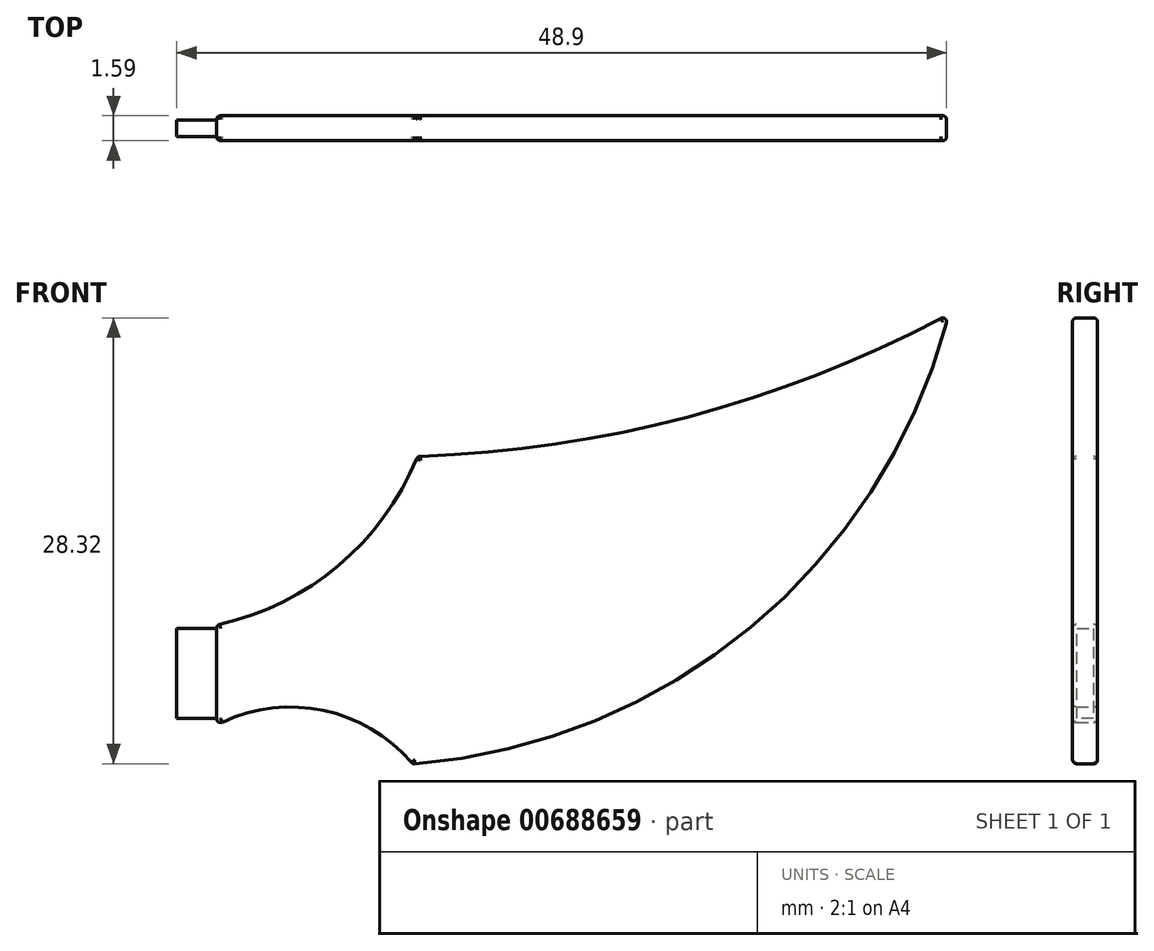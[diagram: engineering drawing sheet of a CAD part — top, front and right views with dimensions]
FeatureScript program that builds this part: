
annotation { "Feature Type Name" : "Feature", "Feature Type Description" : "" }
export const myFeature = defineFeature(function(context is Context, id is Id, definition is map)
    precondition{}
    {
        {
            var Q0;
            Q0=qCreatedBy(makeId("Front.planeOp"),FACE);
            var sketch = newSketch(context, id + "F0", { "sketchPlane" : qUnion([Q0])});
            skLineSegment(sketch, "E0", {"start": v(0, 0) * mm, "end": v(0, 6.35) * mm});
            skLineSegment(sketch, "E1", {"start": v(0, 6.35) * mm, "end": v(12.77, 17.06) * mm, "construction": true});
            skLineSegment(sketch, "E2", {"start": v(12.77, 17.06) * mm, "end": v(46.5, 26.1) * mm, "construction": true});
            skLineSegment(sketch, "E3", {"start": v(12.77, 17.06) * mm, "end": v(12.77, 6.6) * mm, "construction": true});
            skLineSegment(sketch, "E4", {"start": v(46.5, 26.1) * mm, "end": v(12.45, -2.47) * mm, "construction": true});
            skLineSegment(sketch, "E5", {"start": v(46.5, 26.1) * mm, "end": v(46.5, 12.28) * mm, "construction": true});
            skLineSegment(sketch, "E6", {"start": v(0, 0) * mm, "end": v(12.45, -2.47) * mm, "construction": true});
            skArc(sketch, "E7", {"start": v(0, 6.35) * mm, "mid": v(7.72, 10.12) * mm, "end": v(12.77, 17.06) * mm});
            skArc(sketch, "E8", {"start": v(12.77, 17.06) * mm, "mid": v(30.16, 19.63) * mm, "end": v(46.5, 26.1) * mm});
            skArc(sketch, "E9", {"start": v(12.45, -2.47) * mm, "mid": v(34.08, 6.34) * mm, "end": v(46.5, 26.1) * mm});
            skArc(sketch, "E10", {"start": v(12.45, -2.47) * mm, "mid": v(6.66, 0.95) * mm, "end": v(0, 0) * mm});
            skSolve(sketch);
        }
        {
            var Q0;
            Q0=makeQuery(id+"F0.imprint","IMPRINT",FACE,{"disambiguationData":[TD([[makeQuery(id+"F0.imprint","IMPRINT",EDGE,{"derivedFrom":sQuery(id+"F0.wireOp",EDGE,"E0")}),-1.0]])]});
            extrude(context, id + "F1", {"entities" : qUnion([Q0]), "depth" : 1.59 * mm, "offsetDistance" : 25.4 * mm});
        }
        {
            var Q0;
            Q0=makeQuery(id+"F1.opExtrude","CAP_EDGE",EDGE,{"disambiguationData":[OSD([sQuery(id+"F0.wireOp",EDGE,"E7")])],"isStart":true});
            var Q1;
            Q1=makeQuery(id+"F1.opExtrude","CAP_EDGE",EDGE,{"disambiguationData":[OSD([sQuery(id+"F0.wireOp",EDGE,"E7")])],"isStart":false});
            var Q2;
            Q2=makeQuery(id+"F1.opExtrude","CAP_FACE",FACE,{"disambiguationData":[OSD([sQuery(id+"F0.wireOp",EDGE,"E0"),sQuery(id+"F0.wireOp",EDGE,"E7"),sQuery(id+"F0.wireOp",EDGE,"E8"),sQuery(id+"F0.wireOp",EDGE,"E9"),sQuery(id+"F0.wireOp",EDGE,"E10")])],"isStart":true});
            var Q3;
            Q3=makeQuery(id+"F1.opExtrude","CAP_FACE",FACE,{"disambiguationData":[OSD([sQuery(id+"F0.wireOp",EDGE,"E0"),sQuery(id+"F0.wireOp",EDGE,"E7"),sQuery(id+"F0.wireOp",EDGE,"E8"),sQuery(id+"F0.wireOp",EDGE,"E9"),sQuery(id+"F0.wireOp",EDGE,"E10")])],"isStart":false});
            fillet(context, id + "F2", {"entities" : qUnion([Q0, Q1, Q2, Q3]), "radius" : 0.25 * mm, "tangentPropagation" : true, "allowEdgeOverflow" : false});
        }
        {
            var Q0;
            Q0=makeQuery(id+"F1.opExtrude","SWEPT_EDGE",EDGE,{"disambiguationData":[OSD([sQuery(id+"F0.wireOp",EDGE,"E0"),sQuery(id+"F0.wireOp",EDGE,"E7")])]});
            var Q1;
            Q1=makeQuery(id+"F1.opExtrude","SWEPT_EDGE",EDGE,{"disambiguationData":[OSD([sQuery(id+"F0.wireOp",EDGE,"E0"),sQuery(id+"F0.wireOp",EDGE,"E10")])]});
            var Q2;
            Q2=makeQuery(id+"F1.opExtrude","SWEPT_EDGE",EDGE,{"disambiguationData":[OSD([sQuery(id+"F0.wireOp",EDGE,"E9"),sQuery(id+"F0.wireOp",EDGE,"E10")])]});
            var Q3;
            Q3=makeQuery(id+"F1.opExtrude","SWEPT_EDGE",EDGE,{"disambiguationData":[OSD([sQuery(id+"F0.wireOp",EDGE,"E7"),sQuery(id+"F0.wireOp",EDGE,"E8")])]});
            var Q4;
            Q4=makeQuery(id+"F1.opExtrude","SWEPT_EDGE",EDGE,{"disambiguationData":[OSD([sQuery(id+"F0.wireOp",EDGE,"E8"),sQuery(id+"F0.wireOp",EDGE,"E9")])]});
            fillet(context, id + "F3", {"entities" : qUnion([Q0, Q1, Q2, Q3, Q4]), "radius" : 0.25 * mm, "tangentPropagation" : true, "allowEdgeOverflow" : false});
        }
        {
            var Q0;
            Q0=makeQuery(id+"F1.opExtrude","SWEPT_FACE",FACE,{"disambiguationData":[OSD([sQuery(id+"F0.wireOp",EDGE,"E0")])]});
            var sketch = newSketch(context, id + "F4", { "sketchPlane" : qUnion([Q0])});
            skLineSegment(sketch, "E11.bottom", {"start": v(0.25, 6.15) * mm, "end": v(1.33, 6.15) * mm});
            skLineSegment(sketch, "E11.top", {"start": v(0.25, 0.4) * mm, "end": v(1.33, 0.4) * mm});
            skLineSegment(sketch, "E11.left", {"start": v(0.25, 6.15) * mm, "end": v(0.25, 0.4) * mm});
            skLineSegment(sketch, "E11.right", {"start": v(1.33, 6.15) * mm, "end": v(1.33, 0.4) * mm});
            skLineSegment(sketch, "E12.0", {"start": v(0.28, 6.12) * mm, "end": v(0.28, 0.43) * mm});
            skLineSegment(sketch, "E12.1", {"start": v(1.3, 6.12) * mm, "end": v(0.28, 6.12) * mm});
            skLineSegment(sketch, "E12.2", {"start": v(1.3, 0.43) * mm, "end": v(1.3, 6.12) * mm});
            skLineSegment(sketch, "E12.3", {"start": v(0.28, 0.43) * mm, "end": v(1.3, 0.43) * mm});
            skSolve(sketch);
        }
        {
            var Q0;
            Q0=makeQuery(id+"F4.imprint","IMPRINT",FACE,{"disambiguationData":[TD([[makeQuery(id+"F4.imprint","IMPRINT",EDGE,{"derivedFrom":sQuery(id+"F4.wireOp",EDGE,"E12.0")}),1.0]])]});
            extrude(context, id + "F5", {"entities" : qUnion([Q0]), "operationType" : NewBodyOperationType.ADD, "depth" : 2.54 * mm, "offsetDistance" : 25.4 * mm});
        }
    });
